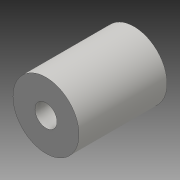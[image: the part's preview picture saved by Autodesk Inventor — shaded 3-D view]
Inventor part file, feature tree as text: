
AUTODESK INVENTOR PART (.ipt)
format: ipt  version: 2016 (Build 200138000, 138)  size: 80,896 bytes
history: native  units: mm
features: sketch x2, extrude x1
ambient origin geometry x8: Origin, YZ Plane, XZ Plane, XY Plane, X Axis, Y Axis, Z Axis, Center Point
bodies: 实体1 (feature_tree)
feature tree (3):
  extrude  "拉伸1"  Depth=5.0mm
  sketch  "草图4"  dims[d2=20.0mm d3=0.0mm]
  sketch  "草图1"  dims[d0=15.0mm d1=5.0mm]
